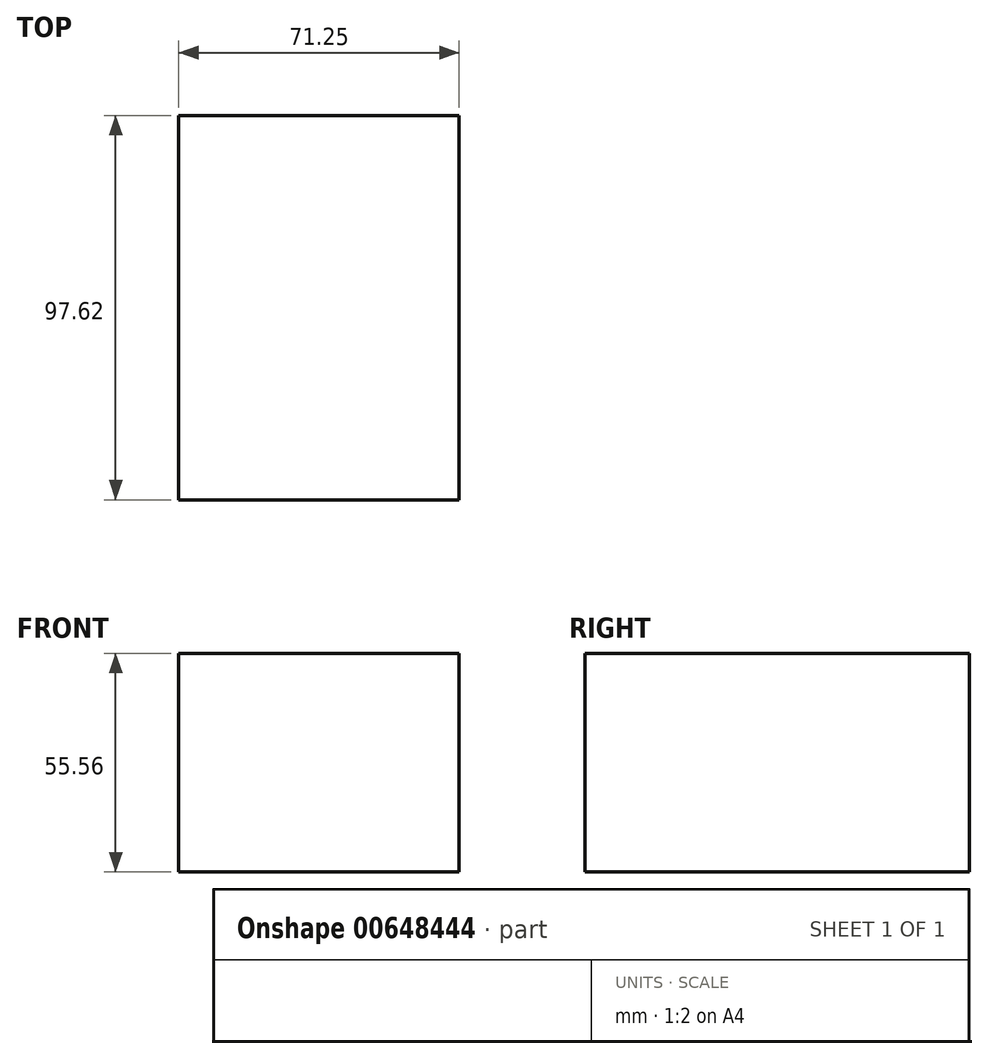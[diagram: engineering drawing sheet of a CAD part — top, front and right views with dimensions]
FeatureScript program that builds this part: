
annotation { "Feature Type Name" : "Feature", "Feature Type Description" : "" }
export const myFeature = defineFeature(function(context is Context, id is Id, definition is map)
    precondition{}
    {
        {
            var Q0;
            Q0=qCreatedBy(makeId("Front.planeOp"),FACE);
            var sketch = newSketch(context, id + "F0", { "sketchPlane" : qUnion([Q0])});
            skLineSegment(sketch, "E0.bottom", {"start": v(71.25, 55.56) * mm, "end": v(0, 55.56) * mm});
            skLineSegment(sketch, "E0.top", {"start": v(71.25, 0) * mm, "end": v(0, 0) * mm});
            skLineSegment(sketch, "E0.left", {"start": v(71.25, 55.56) * mm, "end": v(71.25, 0) * mm});
            skLineSegment(sketch, "E0.right", {"start": v(0, 55.56) * mm, "end": v(0, 0) * mm});
            skSolve(sketch);
        }
        {
            var Q0;
            Q0 = qSketchRegion(id + "F0", true);
            var Q1;
            Q1=makeQuery(id+"F0.imprint","IMPRINT",FACE,{"disambiguationData":[TD([[makeQuery(id+"F0.imprint","IMPRINT",EDGE,{"derivedFrom":sQuery(id+"F0.wireOp",EDGE,"E0.bottom")}),1.0]])]});
            extrude(context, id + "F1", {"entities" : qUnion([Q0, Q1]), "depth" : 97.62 * mm, "offsetDistance" : 25.4 * mm});
        }
    });
